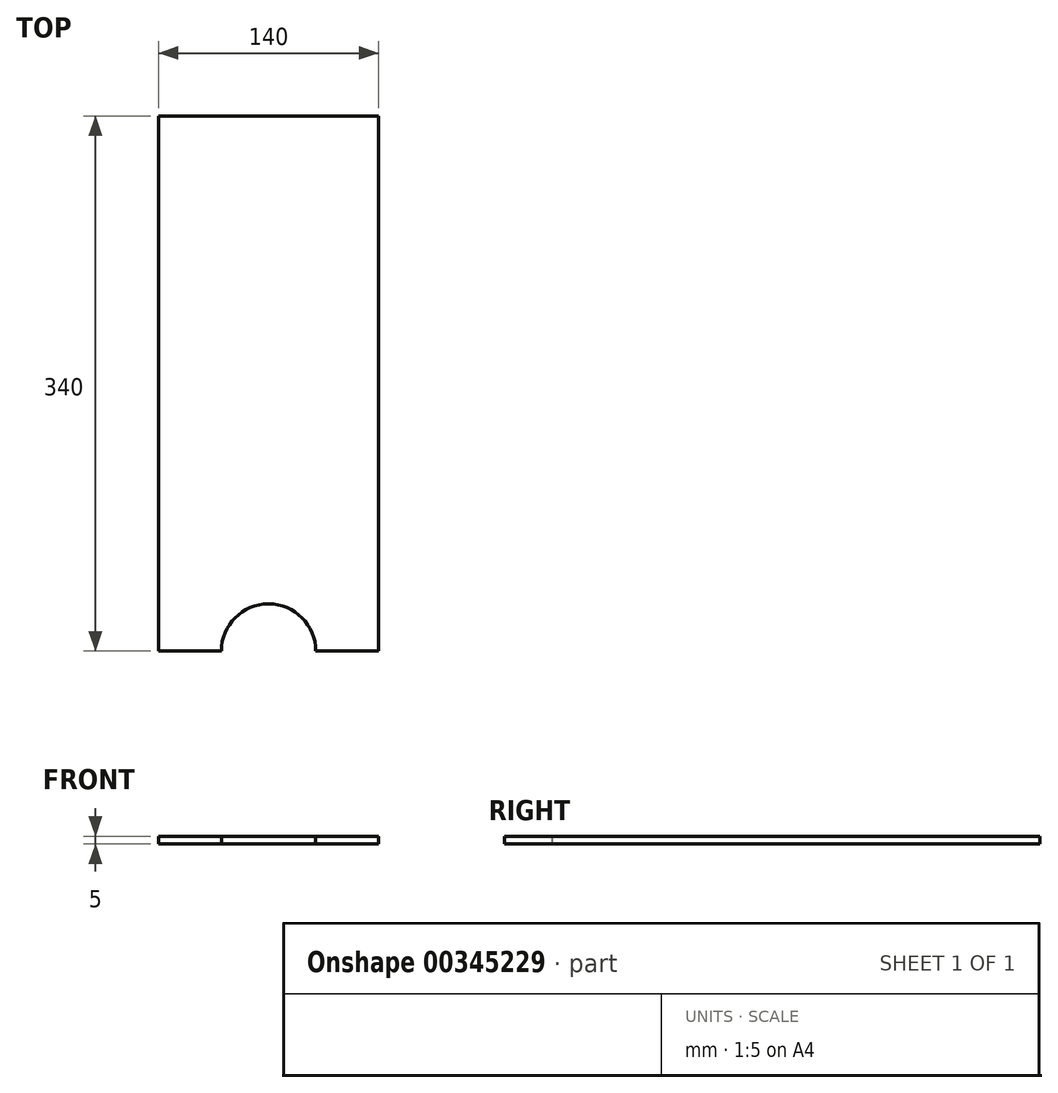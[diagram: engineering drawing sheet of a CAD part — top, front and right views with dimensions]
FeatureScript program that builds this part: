
annotation { "Feature Type Name" : "Feature", "Feature Type Description" : "" }
export const myFeature = defineFeature(function(context is Context, id is Id, definition is map)
    precondition{}
    {
        {
            var Q0;
            Q0=qCreatedBy(makeId("Top.planeOp"),FACE);
            var sketch = newSketch(context, id + "F0", { "sketchPlane" : qUnion([Q0])});
            skLineSegment(sketch, "E0.bottom", {"start": v(-70, 170) * mm, "end": v(70, 170) * mm});
            skLineSegment(sketch, "E0.left", {"start": v(-70, 170) * mm, "end": v(-70, -170) * mm});
            skLineSegment(sketch, "E0.right", {"start": v(70, 170) * mm, "end": v(70, -170) * mm});
            skPoint(sketch, "E0.middle", {"position": v(0, 0) * mm});
            skArc(sketch, "E1", {"start": v(30, -170) * mm, "mid": v(0, -140) * mm, "end": v(-30, -170) * mm});
            skLineSegment(sketch, "E2", {"start": v(-70, -170) * mm, "end": v(-30, -170) * mm});
            skLineSegment(sketch, "E3", {"start": v(70, -170) * mm, "end": v(30, -170) * mm});
            skSolve(sketch);
        }
        {
            var Q0;
            Q0 = qSketchRegion(id + "F0", true);
            extrude(context, id + "F1", {"entities" : qUnion([Q0]), "depth" : 5 * mm});
        }
    });
